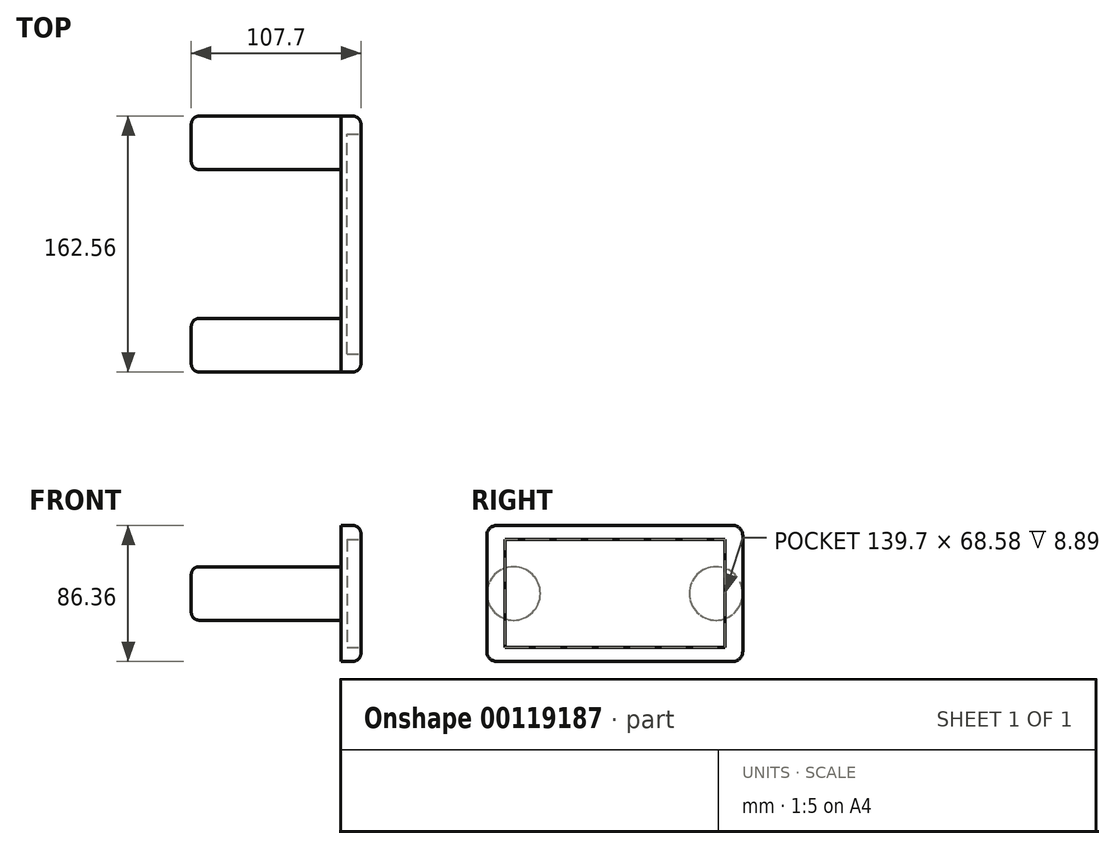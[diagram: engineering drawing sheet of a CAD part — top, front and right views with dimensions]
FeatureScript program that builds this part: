
annotation { "Feature Type Name" : "Feature", "Feature Type Description" : "" }
export const myFeature = defineFeature(function(context is Context, id is Id, definition is map)
    precondition{}
    {
        {
            var Q0;
            Q0=qCreatedBy(makeId("Right.planeOp"),FACE);
            var sketch = newSketch(context, id + "F0", { "sketchPlane" : qUnion([Q0])});
            skLineSegment(sketch, "E0.bottom", {"start": v(-74.93, 43.18) * mm, "end": v(74.93, 43.18) * mm});
            skLineSegment(sketch, "E0.top", {"start": v(-74.93, -43.18) * mm, "end": v(74.93, -43.18) * mm});
            skLineSegment(sketch, "E0.left", {"start": v(-81.28, 36.83) * mm, "end": v(-81.28, -36.83) * mm});
            skLineSegment(sketch, "E0.right", {"start": v(81.28, 36.83) * mm, "end": v(81.28, -36.83) * mm});
            skPoint(sketch, "E0.middle", {"position": v(0, 0) * mm});
            skPoint(sketch, "E1.visualSharp", {"position": v(-81.28, -43.18) * mm});
            skArc(sketch, "E1.filletArc", {"start": v(-81.28, -36.83) * mm, "mid": v(-79.42, -41.32) * mm, "end": v(-74.93, -43.18) * mm});
            skPoint(sketch, "E2.visualSharp", {"position": v(-81.28, 43.18) * mm});
            skArc(sketch, "E2.filletArc", {"start": v(-74.93, 43.18) * mm, "mid": v(-79.42, 41.32) * mm, "end": v(-81.28, 36.83) * mm});
            skPoint(sketch, "E3.visualSharp", {"position": v(81.28, 43.18) * mm});
            skArc(sketch, "E3.filletArc", {"start": v(81.28, 36.83) * mm, "mid": v(79.42, 41.32) * mm, "end": v(74.93, 43.18) * mm});
            skPoint(sketch, "E4.visualSharp", {"position": v(81.28, -43.18) * mm});
            skArc(sketch, "E4.filletArc", {"start": v(74.93, -43.18) * mm, "mid": v(79.42, -41.32) * mm, "end": v(81.28, -36.83) * mm});
            skSolve(sketch);
        }
        {
            var Q0;
            Q0=makeQuery(id+"F0.imprint","IMPRINT",FACE,{"disambiguationData":[TD([[makeQuery(id+"F0.imprint","IMPRINT",EDGE,{"derivedFrom":sQuery(id+"F0.wireOp",EDGE,"E0.bottom")}),-1.0]])]});
            extrude(context, id + "F1", {"entities" : qUnion([Q0]), "depth" : 12.7 * mm});
        }
        {
            var Q0;
            Q0=makeQuery(id+"F1.opExtrude","CAP_FACE",FACE,{"disambiguationData":[OSD([sQuery(id+"F0.wireOp",EDGE,"E0.bottom"),sQuery(id+"F0.wireOp",EDGE,"E0.top"),sQuery(id+"F0.wireOp",EDGE,"E0.left"),sQuery(id+"F0.wireOp",EDGE,"E0.right")])],"isStart":false});
            var sketch = newSketch(context, id + "F2", { "sketchPlane" : qUnion([Q0])});
            skLineSegment(sketch, "E5.bottom", {"start": v(-69.85, 34.3) * mm, "end": v(69.85, 34.3) * mm});
            skLineSegment(sketch, "E5.top", {"start": v(-69.85, -34.3) * mm, "end": v(69.85, -34.3) * mm});
            skLineSegment(sketch, "E5.left", {"start": v(-69.85, 34.3) * mm, "end": v(-69.85, -34.3) * mm});
            skLineSegment(sketch, "E5.right", {"start": v(69.85, 34.3) * mm, "end": v(69.85, -34.3) * mm});
            skPoint(sketch, "E5.middle", {"position": v(0, 0) * mm});
            skSolve(sketch);
        }
        {
            var Q0;
            Q0=makeQuery(id+"F2.imprint","IMPRINT",FACE,{"disambiguationData":[TD([[makeQuery(id+"F2.imprint","IMPRINT",EDGE,{"derivedFrom":sQuery(id+"F2.wireOp",EDGE,"E5.bottom")}),-1.0]])]});
            extrude(context, id + "F3", {"entities" : qUnion([Q0]), "operationType" : NewBodyOperationType.REMOVE, "oppositeDirection" : true, "depth" : 8.9 * mm});
        }
        {
            var Q0;
            Q0=makeQuery(id+"F1.opExtrude","CAP_EDGE",EDGE,{"disambiguationData":[OSD([sQuery(id+"F0.wireOp",EDGE,"E0.right")])],"isStart":false});
            var Q1;
            Q1=makeQuery(id+"F1.opExtrude","CAP_EDGE",EDGE,{"disambiguationData":[OSD([sQuery(id+"F0.wireOp",EDGE,"E0.bottom")])],"isStart":false});
            var Q2;
            Q2=makeQuery(id+"F1.opExtrude","CAP_EDGE",EDGE,{"disambiguationData":[OSD([sQuery(id+"F0.wireOp",EDGE,"E0.left")])],"isStart":false});
            var Q3;
            Q3=makeQuery(id+"F1.opExtrude","CAP_EDGE",EDGE,{"disambiguationData":[OSD([sQuery(id+"F0.wireOp",EDGE,"E0.top")])],"isStart":false});
            fillet(context, id + "F4", {"entities" : qUnion([Q0, Q1, Q2, Q3]), "radius" : 5.08 * mm, "tangentPropagation" : true, "allowEdgeOverflow" : false});
        }
        {
            var Q0;
            Q0=makeQuery(id+"F1.opExtrude","CAP_FACE",FACE,{"disambiguationData":[OSD([sQuery(id+"F0.wireOp",EDGE,"E0.bottom"),sQuery(id+"F0.wireOp",EDGE,"E0.top"),sQuery(id+"F0.wireOp",EDGE,"E0.left"),sQuery(id+"F0.wireOp",EDGE,"E0.right"),sQuery(id+"F0.wireOp",EDGE,"E1.filletArc"),sQuery(id+"F0.wireOp",EDGE,"E2.filletArc"),sQuery(id+"F0.wireOp",EDGE,"E3.filletArc"),sQuery(id+"F0.wireOp",EDGE,"E4.filletArc")])],"isStart":true});
            var sketch = newSketch(context, id + "F5", { "sketchPlane" : qUnion([Q0])});
            skCircle(sketch, "E6", {"center": v(-64.28, 0) * mm, "radius": 17 * mm});
            skCircle(sketch, "E7", {"center": v(64.28, 0) * mm, "radius": 17 * mm});
            skPoint(sketch, "E7.centerSnap0", {"position": v(-81.28, 0) * mm});
            skSolve(sketch);
        }
        {
            var Q0;
            Q0 = qSketchRegion(id + "F5", true);
            extrude(context, id + "F6", {"entities" : qUnion([Q0]), "operationType" : NewBodyOperationType.ADD, "depth" : 95 * mm});
        }
        {
            var Q0;
            Q0=makeQuery(id+"F6.opExtrude","CAP_EDGE",EDGE,{"disambiguationData":[OSD([sQuery(id+"F5.wireOp",EDGE,"E7")])],"isStart":false});
            var Q1;
            Q1=makeQuery(id+"F6.opExtrude","CAP_EDGE",EDGE,{"disambiguationData":[OSD([sQuery(id+"F5.wireOp",EDGE,"E6")])],"isStart":false});
            fillet(context, id + "F7", {"entities" : qUnion([Q0, Q1]), "radius" : 5.08 * mm, "tangentPropagation" : true, "allowEdgeOverflow" : false});
        }
    });
